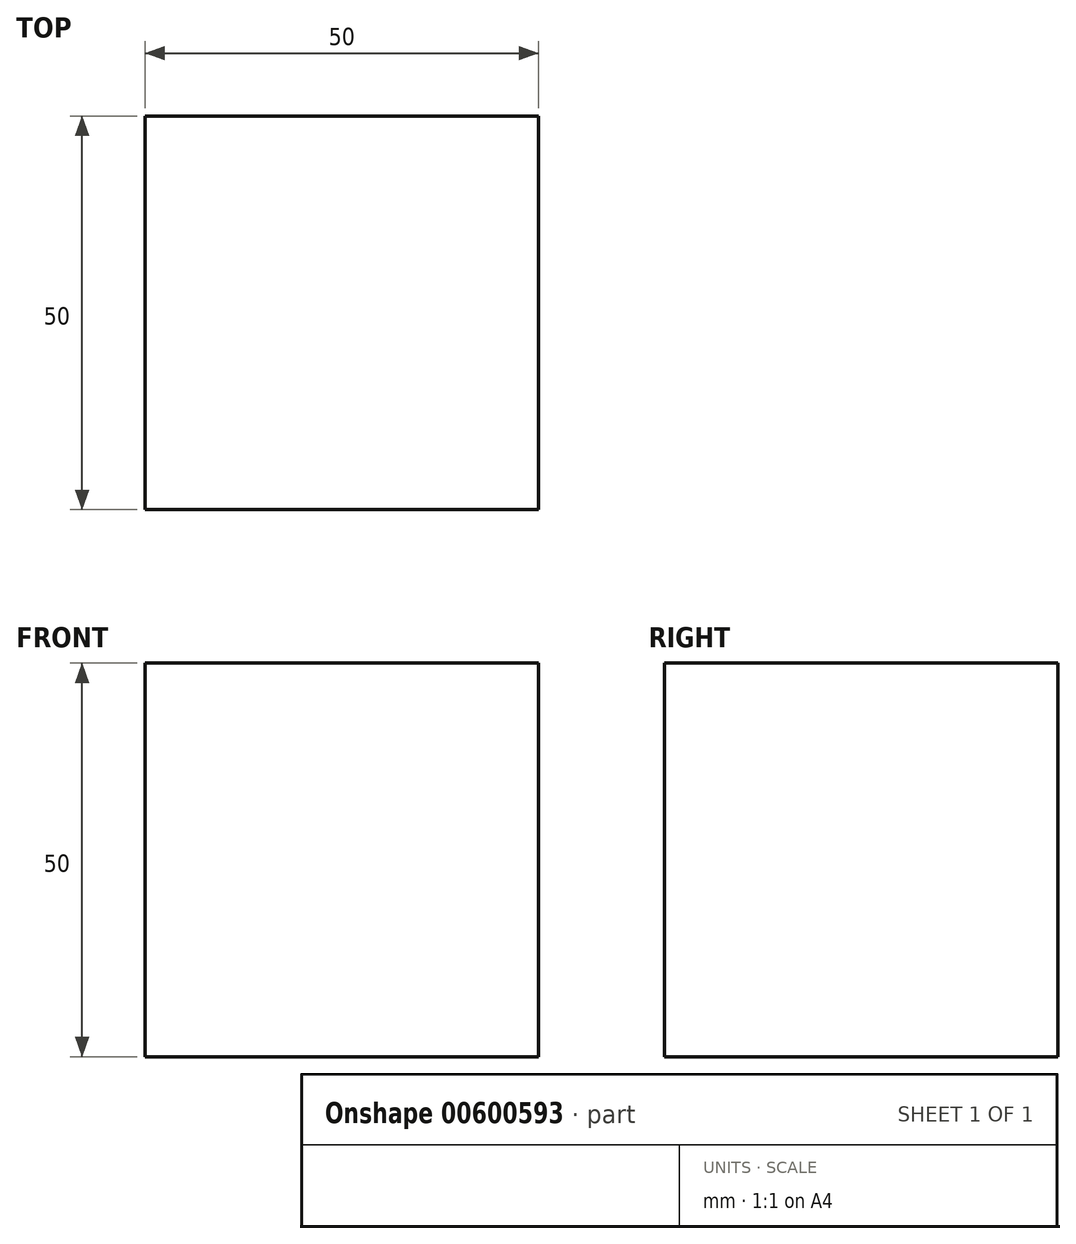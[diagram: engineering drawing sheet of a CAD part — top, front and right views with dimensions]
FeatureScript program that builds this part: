
annotation { "Feature Type Name" : "Feature", "Feature Type Description" : "" }
export const myFeature = defineFeature(function(context is Context, id is Id, definition is map)
    precondition{}
    {
        {
            var Q0;
            Q0=qCreatedBy(makeId("Top.planeOp"),FACE);
            var sketch = newSketch(context, id + "F0", { "sketchPlane" : qUnion([Q0])});
            skLineSegment(sketch, "E0.bottom", {"start": v(-24.23, 27.4) * mm, "end": v(25.77, 27.4) * mm});
            skLineSegment(sketch, "E0.top", {"start": v(-24.23, -22.6) * mm, "end": v(25.77, -22.6) * mm});
            skLineSegment(sketch, "E0.left", {"start": v(-24.23, 27.4) * mm, "end": v(-24.23, -22.6) * mm});
            skLineSegment(sketch, "E0.right", {"start": v(25.77, 27.4) * mm, "end": v(25.77, -22.6) * mm});
            skSolve(sketch);
        }
        {
            var Q0;
            Q0 = qSketchRegion(id + "F0", true);
            extrude(context, id + "F1", {"entities" : qUnion([Q0]), "depth" : 50 * mm, "offsetDistance" : 25 * mm});
        }
    });
